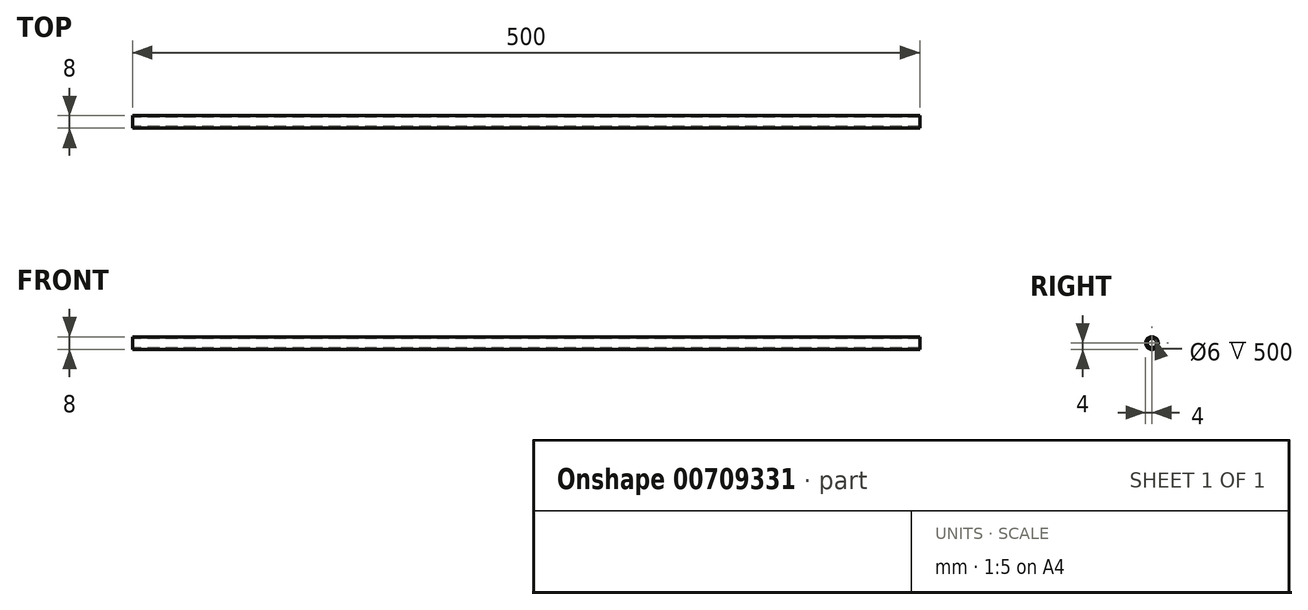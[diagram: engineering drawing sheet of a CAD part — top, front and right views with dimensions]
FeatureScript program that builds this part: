
annotation { "Feature Type Name" : "Feature", "Feature Type Description" : "" }
export const myFeature = defineFeature(function(context is Context, id is Id, definition is map)
    precondition{}
    {
        {
            var Q0;
            Q0=qCreatedBy(makeId("Right.planeOp"),FACE);
            var sketch = newSketch(context, id + "F0", { "sketchPlane" : qUnion([Q0])});
            skCircle(sketch, "E0", {"center": v(0, 0) * mm, "radius": 4 * mm});
            skCircle(sketch, "E1.0", {"center": v(0, 0) * mm, "radius": 3 * mm});
            skSolve(sketch);
        }
        {
            var Q0;
            Q0=makeQuery(id+"F0.imprint","IMPRINT",FACE,{"disambiguationData":[TD([[makeQuery(id+"F0.imprint","IMPRINT",EDGE,{"derivedFrom":sQuery(id+"F0.wireOp",EDGE,"E0")}),1.0]])]});
            extrude(context, id + "F1", {"entities" : qUnion([Q0]), "endBound" : BoundingType.SYMMETRIC, "depth" : 500 * mm, "offsetDistance" : 25 * mm});
        }
    });
